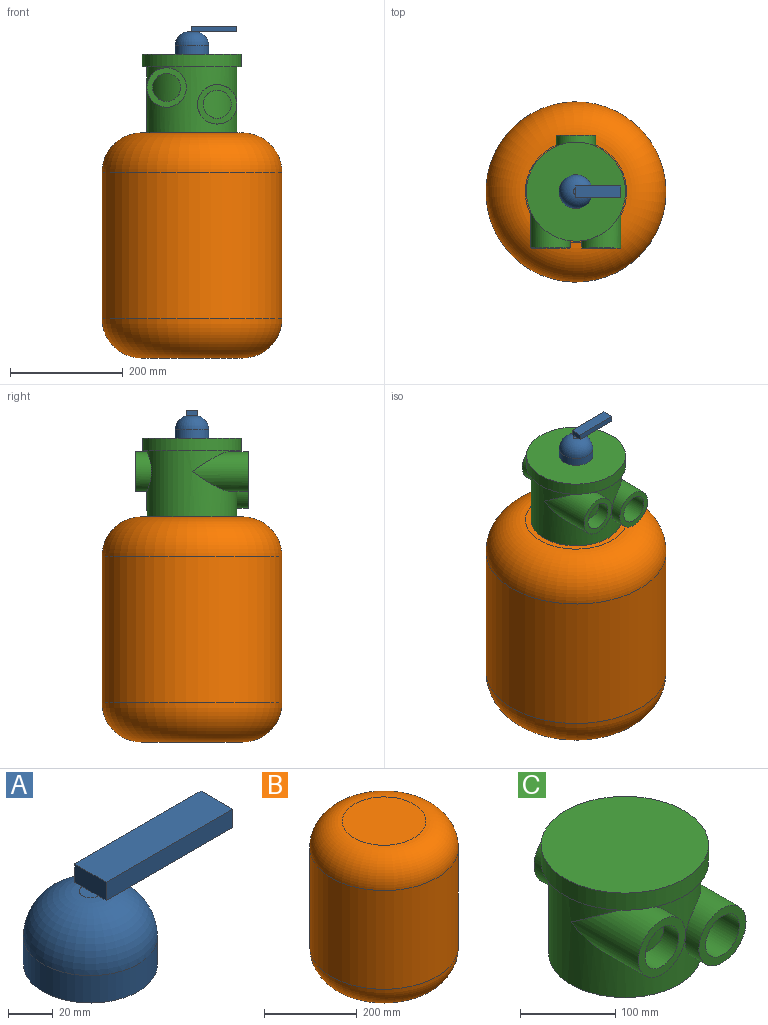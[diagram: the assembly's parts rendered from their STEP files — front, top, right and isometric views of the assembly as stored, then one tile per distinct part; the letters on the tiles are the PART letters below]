
ASSEMBLY  parts=3 mates=2
PART A: 10 faces, bbox 110x60x50 mm
  f0: plane 10x5mm, normal (0,0,1), area 39.3mm2, adj f3,f9
  f1: cylinder r=30mm len=60mm, axis (0,0,-1), area 2827.4mm2, adj f2,f3
  f2: plane 60x60mm, normal (0,0,-1), area 2827.4mm2, adj f1
  f3: torus R=5mm, axis (0,0,1), area 5160.7mm2, adj f0,f1,f4
  f4: plane 80x20mm, normal (0,0,-1), area 1560.7mm2, adj f3,f6,f7,f8,f9
  f5: plane 80x20mm, normal (0,0,1), area 1600mm2, adj f6,f7,f8,f9
  f6: plane 80x10mm, normal (0,-1,0), area 800mm2, adj f4,f5,f8,f9
  f7: plane 80x10mm, normal (0,1,0), area 800mm2, adj f4,f5,f8,f9
  f8: plane 20x10mm, normal (1,0,0), area 200mm2, adj f4,f5,f6,f7
  f9: plane 20x10mm, normal (-1,0,0), area 200mm2, adj f0,f4,f5,f6,f7
PART B: 5 faces, bbox 346.4x346.4x400 mm
  f0: cylinder r=160mm len=320mm, axis (0,0,-1), area 261380.5mm2, adj f3,f4
  f1: plane 180x180mm, normal (0,0,1), area 25446.9mm2, adj f4
  f2: plane 180x180mm, normal (0,0,-1), area 25446.9mm2, adj f3
  f3: torus R=90mm, axis (0,0,1), area 92966.1mm2, adj f0,f2
  f4: torus R=90mm, axis (0,0,1), area 92966.1mm2, adj f0,f1
PART C: 17 faces, bbox 176x200x140 mm
  f0: cylinder r=80mm len=160mm, axis (0,0,-1), area 44413.5mm2, adj f1,f3,f7,f11,f14
  f1: plane 160x160mm, normal (0,0,-1), area 20106.2mm2, adj f0
  f2: cylinder r=88mm len=176mm, axis (0,0,1), area 12164.2mm2, adj f3,f4
  f3: plane 176x176mm, normal (0,0,-1), area 4222.3mm2, adj f0,f2
  f4: plane 176x176mm, normal (0,0,1), area 24328.5mm2, adj f2
  f5: cylinder r=25mm len=50mm, axis (0,-1,0), area 3454.4mm2, adj f6,f8
  f6: plane 70x70mm, normal (0,1,0), area 1885mm2, adj f5,f7
  f7: cylinder r=35mm len=70mm, axis (0,-1,0), area 5275mm2, adj f0,f6
  f8: cylinder r=80mm len=50mm, axis (0,0,-1), area 1988.4mm2, adj f5
  f9: cylinder r=25mm len=61.27mm, axis (0,1,0), area 5926.6mm2, adj f10,f12
  f10: plane 70x70mm, normal (0,-1,0), area 1885mm2, adj f9,f11
  f11: cylinder r=35mm len=100mm, axis (0,1,0), area 9565.8mm2, adj f0,f10
  f12: cylinder r=80mm len=50mm, axis (0,0,-1), area 2501.1mm2, adj f9
  f13: cylinder r=25mm len=61.27mm, axis (0,1,0), area 5923.6mm2, adj f15,f16
  f14: cylinder r=35mm len=100mm, axis (0,1,0), area 9565.8mm2, adj f0,f15
  f15: plane 70x70mm, normal (0,-1,0), area 1885mm2, adj f13,f14
  f16: cylinder r=80mm len=50mm, axis (0,0,-1), area 2499.8mm2, adj f13
PLACE A at identity
PLACE B at identity
PLACE C at identity
MATE fastened A.f1 <-> C.f0  axis (0,0,-1) through (0,0,340)mm
MATE fastened C.f0 <-> B.f0  axis (0,0,-1) through (0,0,200)mm
